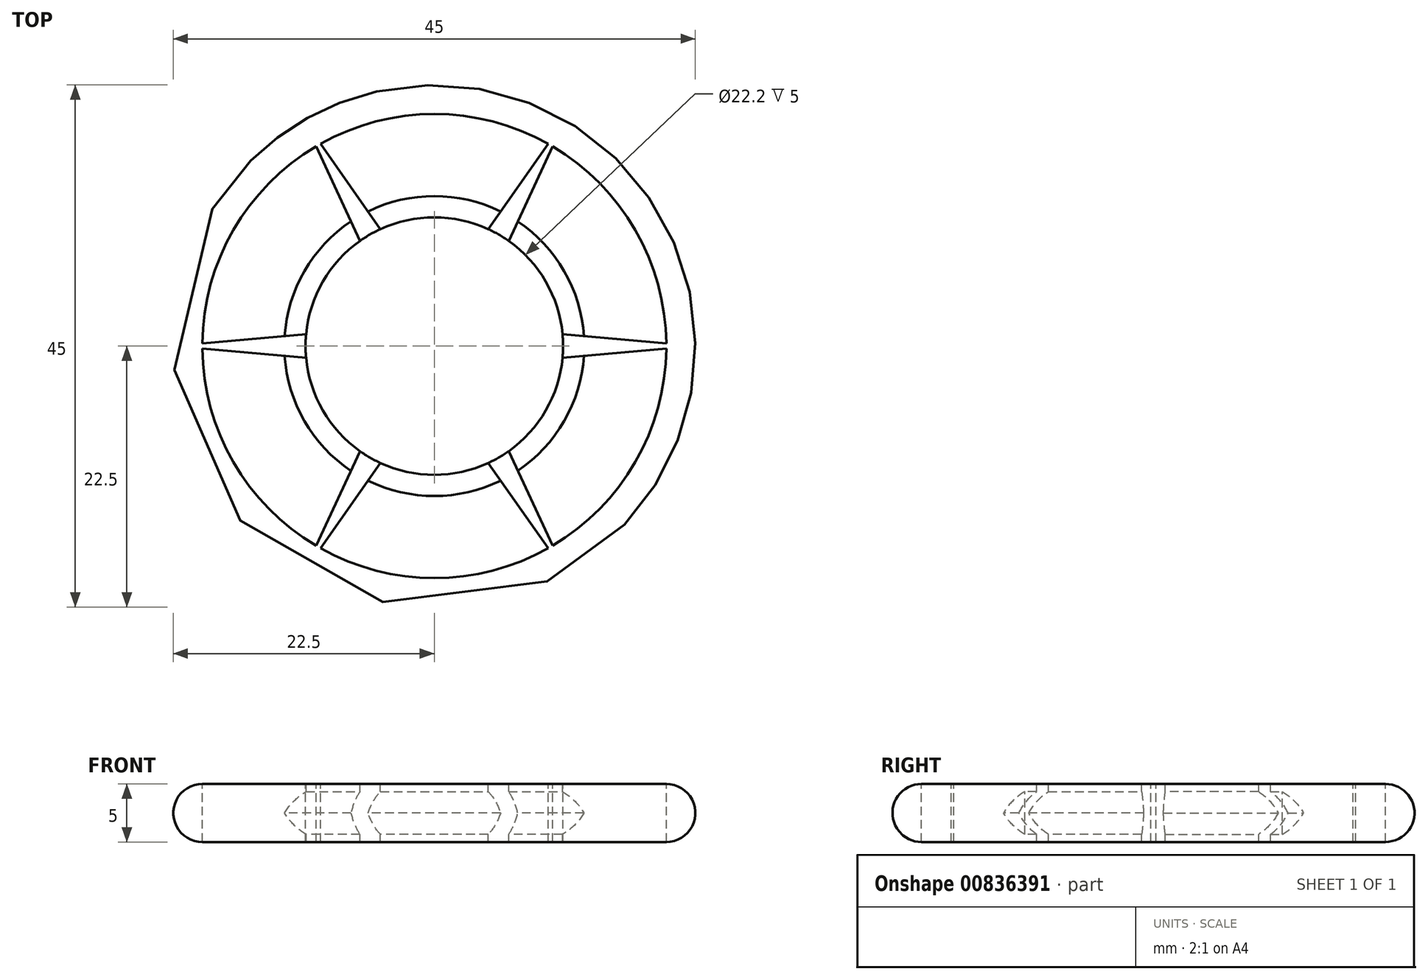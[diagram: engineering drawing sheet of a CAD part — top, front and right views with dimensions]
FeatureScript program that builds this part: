
annotation { "Feature Type Name" : "Feature", "Feature Type Description" : "" }
export const myFeature = defineFeature(function(context is Context, id is Id, definition is map)
    precondition{}
    {
        {
            var Q0;
            Q0=qCreatedBy(makeId("Top.planeOp"),FACE);
            var sketch = newSketch(context, id + "F0", { "sketchPlane" : qUnion([Q0])});
            skCircle(sketch, "E0", {"center": v(0, 0) * mm, "radius": 22.5 * mm});
            skCircle(sketch, "E1", {"center": v(0, 0) * mm, "radius": 20 * mm});
            skCircle(sketch, "E2", {"center": v(0, 0) * mm, "radius": 11.1 * mm});
            skLineSegment(sketch, "E3", {"start": v(0, 0) * mm, "end": v(-20, 0) * mm});
            skLineSegment(sketch, "E4", {"start": v(0, 0) * mm, "end": v(0, 20) * mm});
            skLineSegment(sketch, "E5", {"start": v(0, 0) * mm, "end": v(0, -20) * mm});
            skPoint(sketch, "E6.orphan", {"position": v(0, -2) * mm});
            skPoint(sketch, "E7.end.orphan", {"position": v(0, 2) * mm});
            skLineSegment(sketch, "E8", {"start": v(0, 0) * mm, "end": v(22.5, 0) * mm});
            skLineSegment(sketch, "E9", {"start": v(22.5, 0) * mm, "end": v(0, -2) * mm});
            skLineSegment(sketch, "E10", {"start": v(0, 2) * mm, "end": v(22.5, 0) * mm});
            skLineSegment(sketch, "E11.1.0", {"start": v(-1.73, 1) * mm, "end": v(11.25, 19.49) * mm});
            skLineSegment(sketch, "E11.1.1", {"start": v(11.25, 19.49) * mm, "end": v(1.73, -1) * mm});
            skLineSegment(sketch, "E11.1.2", {"start": v(0, 0) * mm, "end": v(11.25, 19.49) * mm});
            skLineSegment(sketch, "E11.2.0", {"start": v(-1.73, -1) * mm, "end": v(-11.25, 19.49) * mm});
            skLineSegment(sketch, "E11.2.1", {"start": v(-11.25, 19.49) * mm, "end": v(1.73, 1) * mm});
            skLineSegment(sketch, "E11.2.2", {"start": v(0, 0) * mm, "end": v(-11.25, 19.49) * mm});
            skLineSegment(sketch, "E11.3.0", {"start": v(0, -2) * mm, "end": v(-22.5, 0) * mm});
            skLineSegment(sketch, "E11.3.1", {"start": v(-22.5, 0) * mm, "end": v(0, 2) * mm});
            skLineSegment(sketch, "E11.3.2", {"start": v(0, 0) * mm, "end": v(-22.5, 0) * mm});
            skLineSegment(sketch, "E11.4.0", {"start": v(1.73, -1) * mm, "end": v(-11.25, -19.49) * mm});
            skLineSegment(sketch, "E11.4.1", {"start": v(-11.25, -19.49) * mm, "end": v(-1.73, 1) * mm});
            skLineSegment(sketch, "E11.4.2", {"start": v(0, 0) * mm, "end": v(-11.25, -19.49) * mm});
            skLineSegment(sketch, "E11.5.0", {"start": v(1.73, 1) * mm, "end": v(11.25, -19.49) * mm});
            skLineSegment(sketch, "E11.5.1", {"start": v(11.25, -19.49) * mm, "end": v(-1.73, -1) * mm});
            skLineSegment(sketch, "E11.5.2", {"start": v(0, 0) * mm, "end": v(11.25, -19.49) * mm});
            skCircle(sketch, "E12", {"center": v(0, 0) * mm, "radius": 13.6 * mm});
            skSolve(sketch);
        }
        {
            var Q0;
            {var subQ0=sQuery(id+"F0.wireOp",EDGE,"E11.2.0");var subQ1=sQuery(id+"F0.wireOp",EDGE,"E2");var subQ2=makeQuery(id+"F0.imprint","INTERSECT",VERTEX,{"derivedFrom":[subQ1,subQ0]});Q0=makeQuery(id+"F0.imprint","IMPRINT",FACE,{"disambiguationData":[TD([[makeQuery(id+"F0.imprint","IMPRINT",EDGE,{"disambiguationData":[TD([[subQ2,-1.0]])],"derivedFrom":subQ1}),-1.0]])]});}
            var Q1;
            {var subQ0=sQuery(id+"F0.wireOp",EDGE,"E11.3.1");var subQ1=sQuery(id+"F0.wireOp",EDGE,"E2");var subQ2=makeQuery(id+"F0.imprint","INTERSECT",VERTEX,{"derivedFrom":[subQ1,subQ0]});Q1=makeQuery(id+"F0.imprint","IMPRINT",FACE,{"disambiguationData":[TD([[makeQuery(id+"F0.imprint","IMPRINT",EDGE,{"disambiguationData":[TD([[subQ2,-1.0]])],"derivedFrom":subQ1}),-1.0]])]});}
            var Q2;
            {var subQ0=sQuery(id+"F0.wireOp",EDGE,"E11.3.2");var subQ1=sQuery(id+"F0.wireOp",EDGE,"E2");var subQ2=makeQuery(id+"F0.imprint","INTERSECT",VERTEX,{"derivedFrom":[subQ1,subQ0]});Q2=makeQuery(id+"F0.imprint","IMPRINT",FACE,{"disambiguationData":[TD([[makeQuery(id+"F0.imprint","IMPRINT",EDGE,{"disambiguationData":[TD([[subQ2,-1.0]])],"derivedFrom":subQ1}),-1.0]])]});}
            var Q3;
            {var subQ0=sQuery(id+"F0.wireOp",EDGE,"E11.3.0");var subQ1=sQuery(id+"F0.wireOp",EDGE,"E2");var subQ2=makeQuery(id+"F0.imprint","INTERSECT",VERTEX,{"derivedFrom":[subQ1,subQ0]});Q3=makeQuery(id+"F0.imprint","IMPRINT",FACE,{"disambiguationData":[TD([[makeQuery(id+"F0.imprint","IMPRINT",EDGE,{"disambiguationData":[TD([[subQ2,-1.0]])],"derivedFrom":subQ1}),-1.0]])]});}
            var Q4;
            {var subQ0=sQuery(id+"F0.wireOp",EDGE,"E11.4.1");var subQ1=sQuery(id+"F0.wireOp",EDGE,"E2");var subQ2=makeQuery(id+"F0.imprint","INTERSECT",VERTEX,{"derivedFrom":[subQ1,subQ0]});Q4=makeQuery(id+"F0.imprint","IMPRINT",FACE,{"disambiguationData":[TD([[makeQuery(id+"F0.imprint","IMPRINT",EDGE,{"disambiguationData":[TD([[subQ2,-1.0]])],"derivedFrom":subQ1}),-1.0]])]});}
            var Q5;
            {var subQ0=sQuery(id+"F0.wireOp",EDGE,"E11.4.2");var subQ1=sQuery(id+"F0.wireOp",EDGE,"E2");var subQ2=makeQuery(id+"F0.imprint","INTERSECT",VERTEX,{"derivedFrom":[subQ1,subQ0]});Q5=makeQuery(id+"F0.imprint","IMPRINT",FACE,{"disambiguationData":[TD([[makeQuery(id+"F0.imprint","IMPRINT",EDGE,{"disambiguationData":[TD([[subQ2,-1.0]])],"derivedFrom":subQ1}),-1.0]])]});}
            var Q6;
            {var subQ0=sQuery(id+"F0.wireOp",EDGE,"E5");var subQ1=sQuery(id+"F0.wireOp",EDGE,"E2");var subQ2=makeQuery(id+"F0.imprint","INTERSECT",VERTEX,{"derivedFrom":[subQ1,subQ0]});Q6=makeQuery(id+"F0.imprint","IMPRINT",FACE,{"disambiguationData":[TD([[makeQuery(id+"F0.imprint","IMPRINT",EDGE,{"disambiguationData":[TD([[subQ2,-1.0]])],"derivedFrom":subQ1}),-1.0]])]});}
            var Q7;
            {var subQ0=sQuery(id+"F0.wireOp",EDGE,"E11.4.0");var subQ1=sQuery(id+"F0.wireOp",EDGE,"E2");var subQ2=makeQuery(id+"F0.imprint","INTERSECT",VERTEX,{"derivedFrom":[subQ1,subQ0]});Q7=makeQuery(id+"F0.imprint","IMPRINT",FACE,{"disambiguationData":[TD([[makeQuery(id+"F0.imprint","IMPRINT",EDGE,{"disambiguationData":[TD([[subQ2,-1.0]])],"derivedFrom":subQ1}),-1.0]])]});}
            var Q8;
            {var subQ0=sQuery(id+"F0.wireOp",EDGE,"E11.5.1");var subQ1=sQuery(id+"F0.wireOp",EDGE,"E2");var subQ2=makeQuery(id+"F0.imprint","INTERSECT",VERTEX,{"derivedFrom":[subQ1,subQ0]});Q8=makeQuery(id+"F0.imprint","IMPRINT",FACE,{"disambiguationData":[TD([[makeQuery(id+"F0.imprint","IMPRINT",EDGE,{"disambiguationData":[TD([[subQ2,-1.0]])],"derivedFrom":subQ1}),-1.0]])]});}
            var Q9;
            {var subQ0=sQuery(id+"F0.wireOp",EDGE,"E11.5.2");var subQ1=sQuery(id+"F0.wireOp",EDGE,"E2");var subQ2=makeQuery(id+"F0.imprint","INTERSECT",VERTEX,{"derivedFrom":[subQ1,subQ0]});Q9=makeQuery(id+"F0.imprint","IMPRINT",FACE,{"disambiguationData":[TD([[makeQuery(id+"F0.imprint","IMPRINT",EDGE,{"disambiguationData":[TD([[subQ2,-1.0]])],"derivedFrom":subQ1}),-1.0]])]});}
            var Q10;
            {var subQ0=sQuery(id+"F0.wireOp",EDGE,"E11.5.0");var subQ1=sQuery(id+"F0.wireOp",EDGE,"E2");var subQ2=makeQuery(id+"F0.imprint","INTERSECT",VERTEX,{"derivedFrom":[subQ1,subQ0]});Q10=makeQuery(id+"F0.imprint","IMPRINT",FACE,{"disambiguationData":[TD([[makeQuery(id+"F0.imprint","IMPRINT",EDGE,{"disambiguationData":[TD([[subQ2,-1.0]])],"derivedFrom":subQ1}),-1.0]])]});}
            var Q11;
            {var subQ0=sQuery(id+"F0.wireOp",EDGE,"E8");var subQ1=sQuery(id+"F0.wireOp",EDGE,"E2");var subQ2=makeQuery(id+"F0.imprint","INTERSECT",VERTEX,{"derivedFrom":[subQ1,subQ0]});Q11=makeQuery(id+"F0.imprint","IMPRINT",FACE,{"disambiguationData":[TD([[makeQuery(id+"F0.imprint","IMPRINT",EDGE,{"disambiguationData":[TD([[subQ2,1.0]])],"derivedFrom":subQ1}),-1.0]])]});}
            var Q12;
            {var subQ0=sQuery(id+"F0.wireOp",EDGE,"E10");var subQ1=sQuery(id+"F0.wireOp",EDGE,"E2");var subQ2=makeQuery(id+"F0.imprint","INTERSECT",VERTEX,{"derivedFrom":[subQ1,subQ0]});Q12=makeQuery(id+"F0.imprint","IMPRINT",FACE,{"disambiguationData":[TD([[makeQuery(id+"F0.imprint","IMPRINT",EDGE,{"disambiguationData":[TD([[subQ2,1.0]])],"derivedFrom":subQ1}),-1.0]])]});}
            var Q13;
            {var subQ0=sQuery(id+"F0.wireOp",EDGE,"E10");var subQ1=sQuery(id+"F0.wireOp",EDGE,"E2");var subQ2=makeQuery(id+"F0.imprint","INTERSECT",VERTEX,{"derivedFrom":[subQ1,subQ0]});Q13=makeQuery(id+"F0.imprint","IMPRINT",FACE,{"disambiguationData":[TD([[makeQuery(id+"F0.imprint","IMPRINT",EDGE,{"disambiguationData":[TD([[subQ2,-1.0]])],"derivedFrom":subQ1}),-1.0]])]});}
            var Q14;
            {var subQ0=sQuery(id+"F0.wireOp",EDGE,"E11.1.1");var subQ1=sQuery(id+"F0.wireOp",EDGE,"E2");var subQ2=makeQuery(id+"F0.imprint","INTERSECT",VERTEX,{"derivedFrom":[subQ1,subQ0]});Q14=makeQuery(id+"F0.imprint","IMPRINT",FACE,{"disambiguationData":[TD([[makeQuery(id+"F0.imprint","IMPRINT",EDGE,{"disambiguationData":[TD([[subQ2,-1.0]])],"derivedFrom":subQ1}),-1.0]])]});}
            var Q15;
            {var subQ0=sQuery(id+"F0.wireOp",EDGE,"E11.1.2");var subQ1=sQuery(id+"F0.wireOp",EDGE,"E2");var subQ2=makeQuery(id+"F0.imprint","INTERSECT",VERTEX,{"derivedFrom":[subQ1,subQ0]});Q15=makeQuery(id+"F0.imprint","IMPRINT",FACE,{"disambiguationData":[TD([[makeQuery(id+"F0.imprint","IMPRINT",EDGE,{"disambiguationData":[TD([[subQ2,-1.0]])],"derivedFrom":subQ1}),-1.0]])]});}
            var Q16;
            {var subQ0=sQuery(id+"F0.wireOp",EDGE,"E11.1.0");var subQ1=sQuery(id+"F0.wireOp",EDGE,"E2");var subQ2=makeQuery(id+"F0.imprint","INTERSECT",VERTEX,{"derivedFrom":[subQ1,subQ0]});Q16=makeQuery(id+"F0.imprint","IMPRINT",FACE,{"disambiguationData":[TD([[makeQuery(id+"F0.imprint","IMPRINT",EDGE,{"disambiguationData":[TD([[subQ2,-1.0]])],"derivedFrom":subQ1}),-1.0]])]});}
            var Q17;
            {var subQ0=sQuery(id+"F0.wireOp",EDGE,"E4");var subQ1=sQuery(id+"F0.wireOp",EDGE,"E2");var subQ2=makeQuery(id+"F0.imprint","INTERSECT",VERTEX,{"derivedFrom":[subQ1,subQ0]});Q17=makeQuery(id+"F0.imprint","IMPRINT",FACE,{"disambiguationData":[TD([[makeQuery(id+"F0.imprint","IMPRINT",EDGE,{"disambiguationData":[TD([[subQ2,-1.0]])],"derivedFrom":subQ1}),-1.0]])]});}
            var Q18;
            {var subQ0=sQuery(id+"F0.wireOp",EDGE,"E11.2.1");var subQ1=sQuery(id+"F0.wireOp",EDGE,"E2");var subQ2=makeQuery(id+"F0.imprint","INTERSECT",VERTEX,{"derivedFrom":[subQ1,subQ0]});Q18=makeQuery(id+"F0.imprint","IMPRINT",FACE,{"disambiguationData":[TD([[makeQuery(id+"F0.imprint","IMPRINT",EDGE,{"disambiguationData":[TD([[subQ2,-1.0]])],"derivedFrom":subQ1}),-1.0]])]});}
            var Q19;
            {var subQ0=sQuery(id+"F0.wireOp",EDGE,"E11.2.2");var subQ1=sQuery(id+"F0.wireOp",EDGE,"E2");var subQ2=makeQuery(id+"F0.imprint","INTERSECT",VERTEX,{"derivedFrom":[subQ1,subQ0]});Q19=makeQuery(id+"F0.imprint","IMPRINT",FACE,{"disambiguationData":[TD([[makeQuery(id+"F0.imprint","IMPRINT",EDGE,{"disambiguationData":[TD([[subQ2,-1.0]])],"derivedFrom":subQ1}),-1.0]])]});}
            var Q20;
            {var subQ0=sQuery(id+"F0.wireOp",EDGE,"E11.2.0");var subQ5=sQuery(id+"F0.wireOp",EDGE,"E1");var subQ6=makeQuery(id+"F0.imprint","INTERSECT",VERTEX,{"derivedFrom":[subQ5,subQ0]});Q20=makeQuery(id+"F0.imprint","IMPRINT",FACE,{"disambiguationData":[TD([[makeQuery(id+"F0.imprint","IMPRINT",EDGE,{"disambiguationData":[TD([[subQ6,-1.0]])],"derivedFrom":subQ5}),-1.0]])]});}
            var Q21;
            {var subQ0=sQuery(id+"F0.wireOp",EDGE,"E11.3.0");var subQ5=sQuery(id+"F0.wireOp",EDGE,"E1");var subQ6=makeQuery(id+"F0.imprint","INTERSECT",VERTEX,{"derivedFrom":[subQ5,subQ0]});Q21=makeQuery(id+"F0.imprint","IMPRINT",FACE,{"disambiguationData":[TD([[makeQuery(id+"F0.imprint","IMPRINT",EDGE,{"disambiguationData":[TD([[subQ6,-1.0]])],"derivedFrom":subQ5}),-1.0]])]});}
            var Q22;
            {var subQ0=sQuery(id+"F0.wireOp",EDGE,"E1");var subQ1=makeQuery(id+"F0.imprint","INTERSECT",VERTEX,{"derivedFrom":[subQ0,sQuery(id+"F0.wireOp",EDGE,"E5")]});Q22=makeQuery(id+"F0.imprint","IMPRINT",FACE,{"disambiguationData":[TD([[makeQuery(id+"F0.imprint","IMPRINT",EDGE,{"disambiguationData":[TD([[subQ1,1.0]])],"derivedFrom":subQ0}),-1.0]])]});}
            var Q23;
            {var subQ3=sQuery(id+"F0.wireOp",EDGE,"E11.5.0");var subQ5=sQuery(id+"F0.wireOp",EDGE,"E1");var subQ6=makeQuery(id+"F0.imprint","INTERSECT",VERTEX,{"derivedFrom":[subQ5,subQ3]});Q23=makeQuery(id+"F0.imprint","IMPRINT",FACE,{"disambiguationData":[TD([[makeQuery(id+"F0.imprint","IMPRINT",EDGE,{"disambiguationData":[TD([[subQ6,-1.0]])],"derivedFrom":subQ5}),-1.0]])]});}
            var Q24;
            {var subQ0=sQuery(id+"F0.wireOp",EDGE,"E10");var subQ5=sQuery(id+"F0.wireOp",EDGE,"E1");var subQ6=makeQuery(id+"F0.imprint","INTERSECT",VERTEX,{"derivedFrom":[subQ5,subQ0]});Q24=makeQuery(id+"F0.imprint","IMPRINT",FACE,{"disambiguationData":[TD([[makeQuery(id+"F0.imprint","IMPRINT",EDGE,{"disambiguationData":[TD([[subQ6,-1.0]])],"derivedFrom":subQ5}),-1.0]])]});}
            var Q25;
            {var subQ3=sQuery(id+"F0.wireOp",EDGE,"E1");var subQ7=makeQuery(id+"F0.imprint","INTERSECT",VERTEX,{"derivedFrom":[subQ3,sQuery(id+"F0.wireOp",EDGE,"E4")]});Q25=makeQuery(id+"F0.imprint","IMPRINT",FACE,{"disambiguationData":[TD([[makeQuery(id+"F0.imprint","IMPRINT",EDGE,{"disambiguationData":[TD([[subQ7,1.0]])],"derivedFrom":subQ3}),-1.0]])]});}
            var Q26;
            {var subQ0=sQuery(id+"F0.wireOp",EDGE,"E11.1.1");var subQ1=sQuery(id+"F0.wireOp",EDGE,"E1");var subQ2=makeQuery(id+"F0.imprint","INTERSECT",VERTEX,{"derivedFrom":[subQ1,subQ0]});Q26=makeQuery(id+"F0.imprint","IMPRINT",FACE,{"disambiguationData":[TD([[makeQuery(id+"F0.imprint","IMPRINT",EDGE,{"disambiguationData":[TD([[subQ2,-1.0]])],"derivedFrom":subQ1}),-1.0]])]});}
            var Q27;
            {var subQ0=sQuery(id+"F0.wireOp",EDGE,"E11.1.2");var subQ1=sQuery(id+"F0.wireOp",EDGE,"E1");var subQ2=makeQuery(id+"F0.imprint","INTERSECT",VERTEX,{"derivedFrom":[subQ1,subQ0]});Q27=makeQuery(id+"F0.imprint","IMPRINT",FACE,{"disambiguationData":[TD([[makeQuery(id+"F0.imprint","IMPRINT",EDGE,{"disambiguationData":[TD([[subQ2,-1.0]])],"derivedFrom":subQ1}),-1.0]])]});}
            var Q28;
            {var subQ0=sQuery(id+"F0.wireOp",EDGE,"E11.2.1");var subQ1=sQuery(id+"F0.wireOp",EDGE,"E1");var subQ2=makeQuery(id+"F0.imprint","INTERSECT",VERTEX,{"derivedFrom":[subQ1,subQ0]});Q28=makeQuery(id+"F0.imprint","IMPRINT",FACE,{"disambiguationData":[TD([[makeQuery(id+"F0.imprint","IMPRINT",EDGE,{"disambiguationData":[TD([[subQ2,-1.0]])],"derivedFrom":subQ1}),-1.0]])]});}
            var Q29;
            {var subQ0=sQuery(id+"F0.wireOp",EDGE,"E11.2.2");var subQ1=sQuery(id+"F0.wireOp",EDGE,"E1");var subQ2=makeQuery(id+"F0.imprint","INTERSECT",VERTEX,{"derivedFrom":[subQ1,subQ0]});Q29=makeQuery(id+"F0.imprint","IMPRINT",FACE,{"disambiguationData":[TD([[makeQuery(id+"F0.imprint","IMPRINT",EDGE,{"disambiguationData":[TD([[subQ2,-1.0]])],"derivedFrom":subQ1}),-1.0]])]});}
            var Q30;
            {var subQ0=sQuery(id+"F0.wireOp",EDGE,"E11.3.1");var subQ1=sQuery(id+"F0.wireOp",EDGE,"E1");var subQ2=makeQuery(id+"F0.imprint","INTERSECT",VERTEX,{"derivedFrom":[subQ1,subQ0]});Q30=makeQuery(id+"F0.imprint","IMPRINT",FACE,{"disambiguationData":[TD([[makeQuery(id+"F0.imprint","IMPRINT",EDGE,{"disambiguationData":[TD([[subQ2,-1.0]])],"derivedFrom":subQ1}),-1.0]])]});}
            var Q31;
            {var subQ0=sQuery(id+"F0.wireOp",EDGE,"E11.3.2");var subQ1=sQuery(id+"F0.wireOp",EDGE,"E1");var subQ2=makeQuery(id+"F0.imprint","INTERSECT",VERTEX,{"derivedFrom":[subQ1,subQ0]});Q31=makeQuery(id+"F0.imprint","IMPRINT",FACE,{"disambiguationData":[TD([[makeQuery(id+"F0.imprint","IMPRINT",EDGE,{"disambiguationData":[TD([[subQ2,-1.0]])],"derivedFrom":subQ1}),-1.0]])]});}
            var Q32;
            {var subQ0=sQuery(id+"F0.wireOp",EDGE,"E11.4.2");var subQ1=sQuery(id+"F0.wireOp",EDGE,"E1");var subQ2=makeQuery(id+"F0.imprint","INTERSECT",VERTEX,{"derivedFrom":[subQ1,subQ0]});Q32=makeQuery(id+"F0.imprint","IMPRINT",FACE,{"disambiguationData":[TD([[makeQuery(id+"F0.imprint","IMPRINT",EDGE,{"disambiguationData":[TD([[subQ2,-1.0]])],"derivedFrom":subQ1}),-1.0]])]});}
            var Q33;
            {var subQ0=sQuery(id+"F0.wireOp",EDGE,"E11.4.1");var subQ1=sQuery(id+"F0.wireOp",EDGE,"E1");var subQ2=makeQuery(id+"F0.imprint","INTERSECT",VERTEX,{"derivedFrom":[subQ1,subQ0]});Q33=makeQuery(id+"F0.imprint","IMPRINT",FACE,{"disambiguationData":[TD([[makeQuery(id+"F0.imprint","IMPRINT",EDGE,{"disambiguationData":[TD([[subQ2,-1.0]])],"derivedFrom":subQ1}),-1.0]])]});}
            var Q34;
            {var subQ0=sQuery(id+"F0.wireOp",EDGE,"E11.5.2");var subQ1=sQuery(id+"F0.wireOp",EDGE,"E1");var subQ2=makeQuery(id+"F0.imprint","INTERSECT",VERTEX,{"derivedFrom":[subQ1,subQ0]});Q34=makeQuery(id+"F0.imprint","IMPRINT",FACE,{"disambiguationData":[TD([[makeQuery(id+"F0.imprint","IMPRINT",EDGE,{"disambiguationData":[TD([[subQ2,-1.0]])],"derivedFrom":subQ1}),-1.0]])]});}
            var Q35;
            {var subQ0=sQuery(id+"F0.wireOp",EDGE,"E11.5.1");var subQ1=sQuery(id+"F0.wireOp",EDGE,"E1");var subQ2=makeQuery(id+"F0.imprint","INTERSECT",VERTEX,{"derivedFrom":[subQ1,subQ0]});Q35=makeQuery(id+"F0.imprint","IMPRINT",FACE,{"disambiguationData":[TD([[makeQuery(id+"F0.imprint","IMPRINT",EDGE,{"disambiguationData":[TD([[subQ2,-1.0]])],"derivedFrom":subQ1}),-1.0]])]});}
            var Q36;
            {var subQ0=sQuery(id+"F0.wireOp",EDGE,"E10");var subQ1=sQuery(id+"F0.wireOp",EDGE,"E1");var subQ2=makeQuery(id+"F0.imprint","INTERSECT",VERTEX,{"derivedFrom":[subQ1,subQ0]});Q36=makeQuery(id+"F0.imprint","IMPRINT",FACE,{"disambiguationData":[TD([[makeQuery(id+"F0.imprint","IMPRINT",EDGE,{"disambiguationData":[TD([[subQ2,1.0]])],"derivedFrom":subQ1}),-1.0]])]});}
            var Q37;
            {var subQ0=sQuery(id+"F0.wireOp",EDGE,"E8");var subQ1=sQuery(id+"F0.wireOp",EDGE,"E1");var subQ2=makeQuery(id+"F0.imprint","INTERSECT",VERTEX,{"derivedFrom":[subQ1,subQ0]});Q37=makeQuery(id+"F0.imprint","IMPRINT",FACE,{"disambiguationData":[TD([[makeQuery(id+"F0.imprint","IMPRINT",EDGE,{"disambiguationData":[TD([[subQ2,1.0]])],"derivedFrom":subQ1}),-1.0]])]});}
            var Q38;
            {var subQ0=sQuery(id+"F0.wireOp",EDGE,"E11.3.1");var subQ1=sQuery(id+"F0.wireOp",EDGE,"E1");var subQ2=makeQuery(id+"F0.imprint","INTERSECT",VERTEX,{"derivedFrom":[subQ1,subQ0]});Q38=makeQuery(id+"F0.imprint","IMPRINT",FACE,{"disambiguationData":[TD([[makeQuery(id+"F0.imprint","IMPRINT",EDGE,{"disambiguationData":[TD([[subQ2,-1.0]])],"derivedFrom":subQ1}),1.0]])]});}
            var Q39;
            {var subQ0=sQuery(id+"F0.wireOp",EDGE,"E11.3.2");var subQ1=sQuery(id+"F0.wireOp",EDGE,"E1");var subQ2=makeQuery(id+"F0.imprint","INTERSECT",VERTEX,{"derivedFrom":[subQ1,subQ0]});Q39=makeQuery(id+"F0.imprint","IMPRINT",FACE,{"disambiguationData":[TD([[makeQuery(id+"F0.imprint","IMPRINT",EDGE,{"disambiguationData":[TD([[subQ2,-1.0]])],"derivedFrom":subQ1}),1.0]])]});}
            var Q40;
            {var subQ0=sQuery(id+"F0.wireOp",EDGE,"E11.2.1");var subQ1=sQuery(id+"F0.wireOp",EDGE,"E1");var subQ2=makeQuery(id+"F0.imprint","INTERSECT",VERTEX,{"derivedFrom":[subQ1,subQ0]});Q40=makeQuery(id+"F0.imprint","IMPRINT",FACE,{"disambiguationData":[TD([[makeQuery(id+"F0.imprint","IMPRINT",EDGE,{"disambiguationData":[TD([[subQ2,-1.0]])],"derivedFrom":subQ1}),1.0]])]});}
            var Q41;
            {var subQ0=sQuery(id+"F0.wireOp",EDGE,"E11.2.2");var subQ1=sQuery(id+"F0.wireOp",EDGE,"E1");var subQ2=makeQuery(id+"F0.imprint","INTERSECT",VERTEX,{"derivedFrom":[subQ1,subQ0]});Q41=makeQuery(id+"F0.imprint","IMPRINT",FACE,{"disambiguationData":[TD([[makeQuery(id+"F0.imprint","IMPRINT",EDGE,{"disambiguationData":[TD([[subQ2,-1.0]])],"derivedFrom":subQ1}),1.0]])]});}
            var Q42;
            {var subQ0=sQuery(id+"F0.wireOp",EDGE,"E11.1.1");var subQ1=sQuery(id+"F0.wireOp",EDGE,"E1");var subQ2=makeQuery(id+"F0.imprint","INTERSECT",VERTEX,{"derivedFrom":[subQ1,subQ0]});Q42=makeQuery(id+"F0.imprint","IMPRINT",FACE,{"disambiguationData":[TD([[makeQuery(id+"F0.imprint","IMPRINT",EDGE,{"disambiguationData":[TD([[subQ2,-1.0]])],"derivedFrom":subQ1}),1.0]])]});}
            var Q43;
            {var subQ0=sQuery(id+"F0.wireOp",EDGE,"E11.1.2");var subQ1=sQuery(id+"F0.wireOp",EDGE,"E1");var subQ2=makeQuery(id+"F0.imprint","INTERSECT",VERTEX,{"derivedFrom":[subQ1,subQ0]});Q43=makeQuery(id+"F0.imprint","IMPRINT",FACE,{"disambiguationData":[TD([[makeQuery(id+"F0.imprint","IMPRINT",EDGE,{"disambiguationData":[TD([[subQ2,-1.0]])],"derivedFrom":subQ1}),1.0]])]});}
            var Q44;
            {var subQ0=sQuery(id+"F0.wireOp",EDGE,"E8");var subQ1=sQuery(id+"F0.wireOp",EDGE,"E1");var subQ2=makeQuery(id+"F0.imprint","INTERSECT",VERTEX,{"derivedFrom":[subQ1,subQ0]});Q44=makeQuery(id+"F0.imprint","IMPRINT",FACE,{"disambiguationData":[TD([[makeQuery(id+"F0.imprint","IMPRINT",EDGE,{"disambiguationData":[TD([[subQ2,1.0]])],"derivedFrom":subQ1}),1.0]])]});}
            var Q45;
            {var subQ0=sQuery(id+"F0.wireOp",EDGE,"E10");var subQ1=sQuery(id+"F0.wireOp",EDGE,"E1");var subQ2=makeQuery(id+"F0.imprint","INTERSECT",VERTEX,{"derivedFrom":[subQ1,subQ0]});Q45=makeQuery(id+"F0.imprint","IMPRINT",FACE,{"disambiguationData":[TD([[makeQuery(id+"F0.imprint","IMPRINT",EDGE,{"disambiguationData":[TD([[subQ2,1.0]])],"derivedFrom":subQ1}),1.0]])]});}
            var Q46;
            {var subQ0=sQuery(id+"F0.wireOp",EDGE,"E11.5.1");var subQ1=sQuery(id+"F0.wireOp",EDGE,"E1");var subQ2=makeQuery(id+"F0.imprint","INTERSECT",VERTEX,{"derivedFrom":[subQ1,subQ0]});Q46=makeQuery(id+"F0.imprint","IMPRINT",FACE,{"disambiguationData":[TD([[makeQuery(id+"F0.imprint","IMPRINT",EDGE,{"disambiguationData":[TD([[subQ2,-1.0]])],"derivedFrom":subQ1}),1.0]])]});}
            var Q47;
            {var subQ0=sQuery(id+"F0.wireOp",EDGE,"E11.5.2");var subQ1=sQuery(id+"F0.wireOp",EDGE,"E1");var subQ2=makeQuery(id+"F0.imprint","INTERSECT",VERTEX,{"derivedFrom":[subQ1,subQ0]});Q47=makeQuery(id+"F0.imprint","IMPRINT",FACE,{"disambiguationData":[TD([[makeQuery(id+"F0.imprint","IMPRINT",EDGE,{"disambiguationData":[TD([[subQ2,-1.0]])],"derivedFrom":subQ1}),1.0]])]});}
            var Q48;
            {var subQ0=sQuery(id+"F0.wireOp",EDGE,"E11.4.1");var subQ1=sQuery(id+"F0.wireOp",EDGE,"E1");var subQ2=makeQuery(id+"F0.imprint","INTERSECT",VERTEX,{"derivedFrom":[subQ1,subQ0]});Q48=makeQuery(id+"F0.imprint","IMPRINT",FACE,{"disambiguationData":[TD([[makeQuery(id+"F0.imprint","IMPRINT",EDGE,{"disambiguationData":[TD([[subQ2,-1.0]])],"derivedFrom":subQ1}),1.0]])]});}
            var Q49;
            {var subQ0=sQuery(id+"F0.wireOp",EDGE,"E11.4.2");var subQ1=sQuery(id+"F0.wireOp",EDGE,"E1");var subQ2=makeQuery(id+"F0.imprint","INTERSECT",VERTEX,{"derivedFrom":[subQ1,subQ0]});Q49=makeQuery(id+"F0.imprint","IMPRINT",FACE,{"disambiguationData":[TD([[makeQuery(id+"F0.imprint","IMPRINT",EDGE,{"disambiguationData":[TD([[subQ2,-1.0]])],"derivedFrom":subQ1}),1.0]])]});}
            extrude(context, id + "F1", {"entities" : qUnion([Q0, Q1, Q2, Q3, Q4, Q5, Q6, Q7, Q8, Q9, Q10, Q11, Q12, Q13, Q14, Q15, Q16, Q17, Q18, Q19, Q20, Q21, Q22, Q23, Q24, Q25, Q26, Q27, Q28, Q29, Q30, Q31, Q32, Q33, Q34, Q35, Q36, Q37, Q38, Q39, Q40, Q41, Q42, Q43, Q44, Q45, Q46, Q47, Q48, Q49]), "oppositeDirection" : true, "depth" : 5 * mm, "offsetDistance" : 25 * mm});
        }
        {
            var Q0;
            Q0=makeQuery(id+"F1.opExtrude","CAP_EDGE",EDGE,{"disambiguationData":[OSD([sQuery(id+"F0.wireOp",EDGE,"E0")])],"isStart":true});
            var Q1;
            Q1=makeQuery(id+"F1.opExtrude","CAP_EDGE",EDGE,{"disambiguationData":[OSD([sQuery(id+"F0.wireOp",EDGE,"E0")])],"isStart":false});
            fillet(context, id + "F2", {"entities" : qUnion([Q0, Q1]), "radius" : 2.5 * mm, "tangentPropagation" : true, "allowEdgeOverflow" : false});
        }
        {
            var Q0;
            {var subQ0=sQuery(id+"F0.wireOp",EDGE,"E12");Q0=makeQuery(id+"F1.opExtrude","CAP_EDGE",EDGE,{"disambiguationData":[OSD([subQ0]),TDD([makeQuery(id+"F0.imprint","IMPRINT",EDGE,{"disambiguationData":[TD([[makeQuery(id+"F0.imprint","INTERSECT",VERTEX,{"derivedFrom":[sQuery(id+"F0.wireOp",EDGE,"E9"),subQ0]}),1.0]])],"derivedFrom":subQ0})])],"isStart":true});}
            var Q1;
            {var subQ0=sQuery(id+"F0.wireOp",EDGE,"E12");Q1=makeQuery(id+"F1.opExtrude","CAP_EDGE",EDGE,{"disambiguationData":[OSD([subQ0]),TDD([makeQuery(id+"F0.imprint","IMPRINT",EDGE,{"disambiguationData":[TD([[makeQuery(id+"F0.imprint","INTERSECT",VERTEX,{"derivedFrom":[sQuery(id+"F0.wireOp",EDGE,"E10"),subQ0]}),-1.0]])],"derivedFrom":subQ0})])],"isStart":true});}
            var Q2;
            {var subQ0=sQuery(id+"F0.wireOp",EDGE,"E12");var subQ1=makeQuery(id+"F0.imprint","INTERSECT",VERTEX,{"derivedFrom":[sQuery(id+"F0.wireOp",EDGE,"E4"),subQ0]});Q2=makeQuery(id+"F1.opExtrude","CAP_EDGE",EDGE,{"disambiguationData":[OSD([subQ0]),TDD([makeQuery(id+"F0.imprint","IMPRINT",EDGE,{"disambiguationData":[TD([[subQ1,1.0]])],"derivedFrom":subQ0}),makeQuery(id+"F0.imprint","IMPRINT",EDGE,{"disambiguationData":[TD([[subQ1,-1.0]])],"derivedFrom":subQ0})])],"isStart":true});}
            var Q3;
            {var subQ0=sQuery(id+"F0.wireOp",EDGE,"E12");Q3=makeQuery(id+"F1.opExtrude","CAP_EDGE",EDGE,{"disambiguationData":[OSD([subQ0]),TDD([makeQuery(id+"F0.imprint","IMPRINT",EDGE,{"disambiguationData":[TD([[makeQuery(id+"F0.imprint","INTERSECT",VERTEX,{"derivedFrom":[sQuery(id+"F0.wireOp",EDGE,"E11.2.0"),subQ0]}),-1.0]])],"derivedFrom":subQ0})])],"isStart":true});}
            var Q4;
            {var subQ0=sQuery(id+"F0.wireOp",EDGE,"E12");Q4=makeQuery(id+"F1.opExtrude","CAP_EDGE",EDGE,{"disambiguationData":[OSD([subQ0]),TDD([makeQuery(id+"F0.imprint","IMPRINT",EDGE,{"disambiguationData":[TD([[makeQuery(id+"F0.imprint","INTERSECT",VERTEX,{"derivedFrom":[sQuery(id+"F0.wireOp",EDGE,"E11.3.0"),subQ0]}),-1.0]])],"derivedFrom":subQ0})])],"isStart":true});}
            var Q5;
            {var subQ0=sQuery(id+"F0.wireOp",EDGE,"E12");var subQ1=makeQuery(id+"F0.imprint","INTERSECT",VERTEX,{"derivedFrom":[sQuery(id+"F0.wireOp",EDGE,"E5"),subQ0]});Q5=makeQuery(id+"F1.opExtrude","CAP_EDGE",EDGE,{"disambiguationData":[OSD([subQ0]),TDD([makeQuery(id+"F0.imprint","IMPRINT",EDGE,{"disambiguationData":[TD([[subQ1,1.0]])],"derivedFrom":subQ0}),makeQuery(id+"F0.imprint","IMPRINT",EDGE,{"disambiguationData":[TD([[subQ1,-1.0]])],"derivedFrom":subQ0})])],"isStart":true});}
            var Q6;
            {var subQ0=sQuery(id+"F0.wireOp",EDGE,"E12");var subQ1=makeQuery(id+"F0.imprint","INTERSECT",VERTEX,{"derivedFrom":[sQuery(id+"F0.wireOp",EDGE,"E4"),subQ0]});Q6=makeQuery(id+"F1.opExtrude","CAP_EDGE",EDGE,{"disambiguationData":[OSD([subQ0]),TDD([makeQuery(id+"F0.imprint","IMPRINT",EDGE,{"disambiguationData":[TD([[subQ1,1.0]])],"derivedFrom":subQ0}),makeQuery(id+"F0.imprint","IMPRINT",EDGE,{"disambiguationData":[TD([[subQ1,-1.0]])],"derivedFrom":subQ0})])],"isStart":false});}
            var Q7;
            {var subQ0=sQuery(id+"F0.wireOp",EDGE,"E12");Q7=makeQuery(id+"F1.opExtrude","CAP_EDGE",EDGE,{"disambiguationData":[OSD([subQ0]),TDD([makeQuery(id+"F0.imprint","IMPRINT",EDGE,{"disambiguationData":[TD([[makeQuery(id+"F0.imprint","INTERSECT",VERTEX,{"derivedFrom":[sQuery(id+"F0.wireOp",EDGE,"E10"),subQ0]}),-1.0]])],"derivedFrom":subQ0})])],"isStart":false});}
            var Q8;
            {var subQ0=sQuery(id+"F0.wireOp",EDGE,"E12");Q8=makeQuery(id+"F1.opExtrude","CAP_EDGE",EDGE,{"disambiguationData":[OSD([subQ0]),TDD([makeQuery(id+"F0.imprint","IMPRINT",EDGE,{"disambiguationData":[TD([[makeQuery(id+"F0.imprint","INTERSECT",VERTEX,{"derivedFrom":[sQuery(id+"F0.wireOp",EDGE,"E11.2.0"),subQ0]}),-1.0]])],"derivedFrom":subQ0})])],"isStart":false});}
            var Q9;
            {var subQ0=sQuery(id+"F0.wireOp",EDGE,"E12");Q9=makeQuery(id+"F1.opExtrude","CAP_EDGE",EDGE,{"disambiguationData":[OSD([subQ0]),TDD([makeQuery(id+"F0.imprint","IMPRINT",EDGE,{"disambiguationData":[TD([[makeQuery(id+"F0.imprint","INTERSECT",VERTEX,{"derivedFrom":[sQuery(id+"F0.wireOp",EDGE,"E11.3.0"),subQ0]}),-1.0]])],"derivedFrom":subQ0})])],"isStart":false});}
            var Q10;
            {var subQ0=sQuery(id+"F0.wireOp",EDGE,"E12");var subQ1=makeQuery(id+"F0.imprint","INTERSECT",VERTEX,{"derivedFrom":[sQuery(id+"F0.wireOp",EDGE,"E5"),subQ0]});Q10=makeQuery(id+"F1.opExtrude","CAP_EDGE",EDGE,{"disambiguationData":[OSD([subQ0]),TDD([makeQuery(id+"F0.imprint","IMPRINT",EDGE,{"disambiguationData":[TD([[subQ1,1.0]])],"derivedFrom":subQ0}),makeQuery(id+"F0.imprint","IMPRINT",EDGE,{"disambiguationData":[TD([[subQ1,-1.0]])],"derivedFrom":subQ0})])],"isStart":false});}
            var Q11;
            {var subQ0=sQuery(id+"F0.wireOp",EDGE,"E12");Q11=makeQuery(id+"F1.opExtrude","CAP_EDGE",EDGE,{"disambiguationData":[OSD([subQ0]),TDD([makeQuery(id+"F0.imprint","IMPRINT",EDGE,{"disambiguationData":[TD([[makeQuery(id+"F0.imprint","INTERSECT",VERTEX,{"derivedFrom":[sQuery(id+"F0.wireOp",EDGE,"E9"),subQ0]}),1.0]])],"derivedFrom":subQ0})])],"isStart":false});}
            fillet(context, id + "F3", {"entities" : qUnion([Q0, Q1, Q2, Q3, Q4, Q5, Q6, Q7, Q8, Q9, Q10, Q11]), "radius" : 5 * mm, "tangentPropagation" : true, "allowEdgeOverflow" : false});
        }
    });
